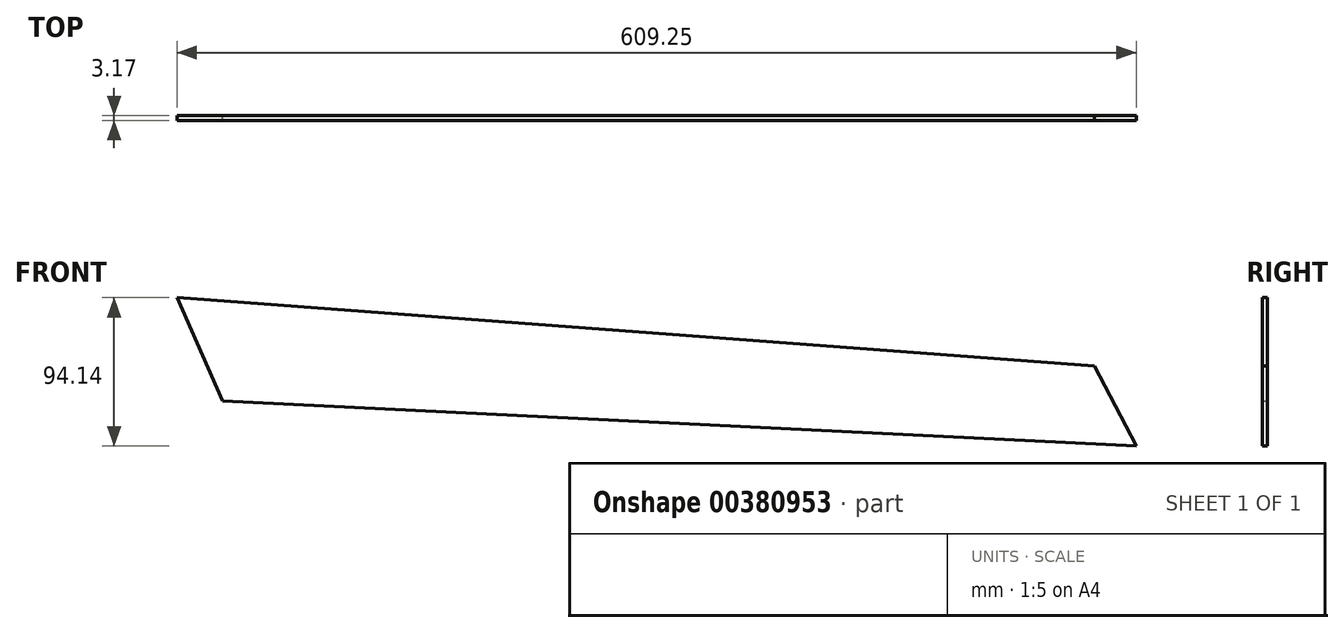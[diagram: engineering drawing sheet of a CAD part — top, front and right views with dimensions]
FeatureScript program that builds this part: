
annotation { "Feature Type Name" : "Feature", "Feature Type Description" : "" }
export const myFeature = defineFeature(function(context is Context, id is Id, definition is map)
    precondition{}
    {
        {
            var Q0;
            Q0=qCreatedBy(makeId("Front.planeOp"),FACE);
            var sketch = newSketch(context, id + "F0", { "sketchPlane" : qUnion([Q0])});
            skLineSegment(sketch, "E0", {"start": v(0, 0) * mm, "end": v(-580.19, 28.67) * mm});
            skLineSegment(sketch, "E1", {"start": v(-580.19, 28.67) * mm, "end": v(-609.25, 94.14) * mm});
            skLineSegment(sketch, "E2", {"start": v(-609.25, 94.14) * mm, "end": v(-26.66, 50.84) * mm});
            skLineSegment(sketch, "E3", {"start": v(-26.66, 50.84) * mm, "end": v(0, 0) * mm});
            skSolve(sketch);
        }
        {
            var Q0;
            Q0=qSketchRegion(id+"F0",true);
            extrude(context, id + "F1", {"entities" : qUnion([Q0]), "depth" : 3.17 * mm});
        }
    });
